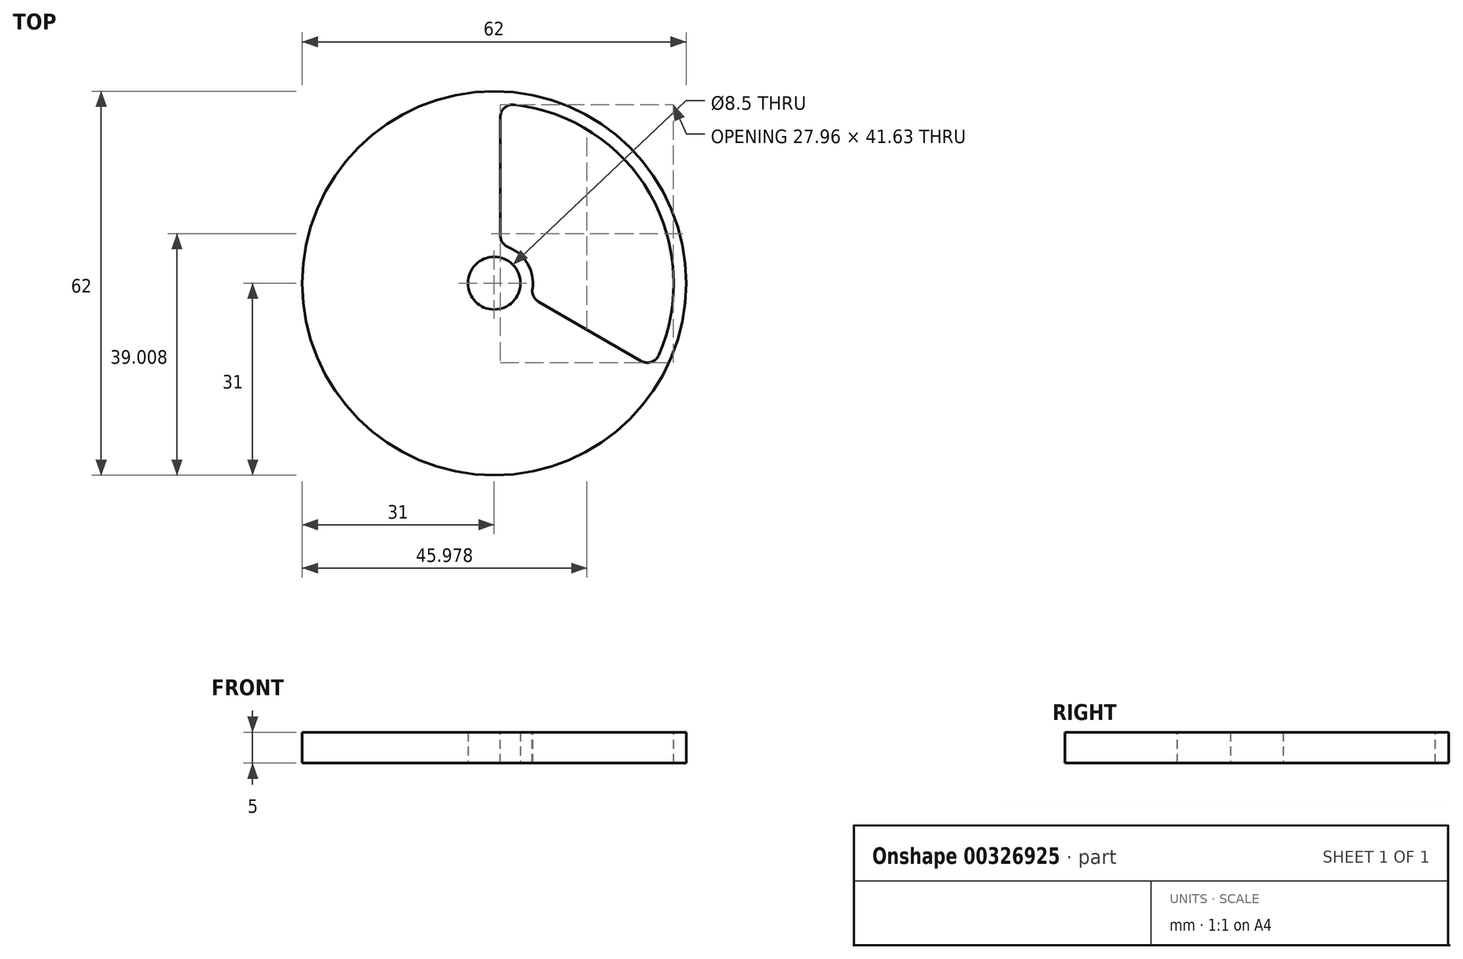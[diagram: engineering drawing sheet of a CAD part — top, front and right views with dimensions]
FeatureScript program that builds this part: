
annotation { "Feature Type Name" : "Feature", "Feature Type Description" : "" }
export const myFeature = defineFeature(function(context is Context, id is Id, definition is map)
    precondition{}
    {
        {
            var Q0;
            Q0=qCreatedBy(makeId("Top.planeOp"),FACE);
            var sketch = newSketch(context, id + "F0", { "sketchPlane" : qUnion([Q0])});
            skCircle(sketch, "E0", {"center": v(0, 0) * mm, "radius": 4.25 * mm});
            skCircle(sketch, "E1", {"center": v(0, 0) * mm, "radius": 31 * mm});
            skSolve(sketch);
        }
        {
            var Q0;
            Q0 = qSketchRegion(id + "F0", true);
            extrude(context, id + "F1", {"entities" : qUnion([Q0]), "depth" : 5 * mm});
        }
        {
            var Q0;
            Q0=makeQuery(id+"F1.opExtrude","CAP_FACE",FACE,{"disambiguationData":[OSD([sQuery(id+"F0.wireOp",EDGE,"E0"),sQuery(id+"F0.wireOp",EDGE,"E1")])],"isStart":false});
            var sketch = newSketch(context, id + "F2", { "sketchPlane" : qUnion([Q0])});
            skArc(sketch, "E2", {"start": v(5.84, -2.22) * mm, "mid": v(5.41, 3.13) * mm, "end": v(1, 6.17) * mm});
            skArc(sketch, "E3", {"start": v(25.6, -13.63) * mm, "mid": v(25.11, 14.5) * mm, "end": v(1, 28.98) * mm});
            skLineSegment(sketch, "E4", {"start": v(1, 6.17) * mm, "end": v(1, 28.98) * mm});
            skLineSegment(sketch, "E5", {"start": v(5.84, -2.22) * mm, "end": v(25.6, -13.63) * mm});
            skLineSegment(sketch, "E6", {"start": v(0, 0) * mm, "end": v(15.82, -9.14) * mm, "construction": true});
            skLineSegment(sketch, "E7", {"start": v(0, 0) * mm, "end": v(0, 20.22) * mm, "construction": true});
            skSolve(sketch);
        }
        {
            var Q0;
            Q0 = qSketchRegion(id + "F2", true);
            extrude(context, id + "F3", {"entities" : qUnion([Q0]), "operationType" : NewBodyOperationType.REMOVE, "oppositeDirection" : true, "depth" : 25 * mm});
        }
        {
            var Q0;
            Q0=makeQuery(id+"FdAd1jSosg7aUJC_1.2.F3.boolean.opBoolean","COPY",EDGE,{"derivedFrom":makeQuery(id+"FdAd1jSosg7aUJC_1.2.F3.opExtrude","SWEPT_EDGE",EDGE,{"disambiguationData":[OSD([sQuery(id+"F2.wireOp",EDGE,"E2"),sQuery(id+"F2.wireOp",EDGE,"E5")])]})});
            var Q1;
            Q1=makeQuery(id+"FdAd1jSosg7aUJC_1.2.F3.boolean.opBoolean","COPY",EDGE,{"derivedFrom":makeQuery(id+"FdAd1jSosg7aUJC_1.2.F3.opExtrude","SWEPT_EDGE",EDGE,{"disambiguationData":[OSD([sQuery(id+"F2.wireOp",EDGE,"E2"),sQuery(id+"F2.wireOp",EDGE,"E4")])]})});
            var Q2;
            Q2=makeQuery(id+"FdAd1jSosg7aUJC_1.1.F3.boolean.opBoolean","COPY",EDGE,{"derivedFrom":makeQuery(id+"FdAd1jSosg7aUJC_1.1.F3.opExtrude","SWEPT_EDGE",EDGE,{"disambiguationData":[OSD([sQuery(id+"F2.wireOp",EDGE,"E2"),sQuery(id+"F2.wireOp",EDGE,"E4")])]})});
            var Q3;
            Q3=makeQuery(id+"FdAd1jSosg7aUJC_1.1.F3.boolean.opBoolean","COPY",EDGE,{"derivedFrom":makeQuery(id+"FdAd1jSosg7aUJC_1.1.F3.opExtrude","SWEPT_EDGE",EDGE,{"disambiguationData":[OSD([sQuery(id+"F2.wireOp",EDGE,"E2"),sQuery(id+"F2.wireOp",EDGE,"E5")])]})});
            var Q4;
            Q4=makeQuery(id+"F3.boolean.opBoolean","COPY",EDGE,{"derivedFrom":makeQuery(id+"F3.opExtrude","SWEPT_EDGE",EDGE,{"disambiguationData":[OSD([sQuery(id+"F2.wireOp",EDGE,"E2"),sQuery(id+"F2.wireOp",EDGE,"E4")])]})});
            var Q5;
            Q5=makeQuery(id+"F3.boolean.opBoolean","COPY",EDGE,{"derivedFrom":makeQuery(id+"F3.opExtrude","SWEPT_EDGE",EDGE,{"disambiguationData":[OSD([sQuery(id+"F2.wireOp",EDGE,"E2"),sQuery(id+"F2.wireOp",EDGE,"E5")])]})});
            var Q6;
            Q6=makeQuery(id+"F3.boolean.opBoolean","COPY",EDGE,{"derivedFrom":makeQuery(id+"F3.opExtrude","SWEPT_EDGE",EDGE,{"disambiguationData":[OSD([sQuery(id+"F2.wireOp",EDGE,"E3"),sQuery(id+"F2.wireOp",EDGE,"E5")])]})});
            var Q7;
            Q7=makeQuery(id+"FdAd1jSosg7aUJC_1.2.F3.boolean.opBoolean","COPY",EDGE,{"derivedFrom":makeQuery(id+"FdAd1jSosg7aUJC_1.2.F3.opExtrude","SWEPT_EDGE",EDGE,{"disambiguationData":[OSD([sQuery(id+"F2.wireOp",EDGE,"E3"),sQuery(id+"F2.wireOp",EDGE,"E4")])]})});
            var Q8;
            Q8=makeQuery(id+"FdAd1jSosg7aUJC_1.2.F3.boolean.opBoolean","COPY",EDGE,{"derivedFrom":makeQuery(id+"FdAd1jSosg7aUJC_1.2.F3.opExtrude","SWEPT_EDGE",EDGE,{"disambiguationData":[OSD([sQuery(id+"F2.wireOp",EDGE,"E3"),sQuery(id+"F2.wireOp",EDGE,"E5")])]})});
            var Q9;
            Q9=makeQuery(id+"FdAd1jSosg7aUJC_1.1.F3.boolean.opBoolean","COPY",EDGE,{"derivedFrom":makeQuery(id+"FdAd1jSosg7aUJC_1.1.F3.opExtrude","SWEPT_EDGE",EDGE,{"disambiguationData":[OSD([sQuery(id+"F2.wireOp",EDGE,"E3"),sQuery(id+"F2.wireOp",EDGE,"E4")])]})});
            var Q10;
            Q10=makeQuery(id+"FdAd1jSosg7aUJC_1.1.F3.boolean.opBoolean","COPY",EDGE,{"derivedFrom":makeQuery(id+"FdAd1jSosg7aUJC_1.1.F3.opExtrude","SWEPT_EDGE",EDGE,{"disambiguationData":[OSD([sQuery(id+"F2.wireOp",EDGE,"E3"),sQuery(id+"F2.wireOp",EDGE,"E5")])]})});
            var Q11;
            Q11=makeQuery(id+"F3.boolean.opBoolean","COPY",EDGE,{"derivedFrom":makeQuery(id+"F3.opExtrude","SWEPT_EDGE",EDGE,{"disambiguationData":[OSD([sQuery(id+"F2.wireOp",EDGE,"E3"),sQuery(id+"F2.wireOp",EDGE,"E4")])]})});
            fillet(context, id + "F4", {"entities" : qUnion([Q0, Q1, Q2, Q3, Q4, Q5, Q6, Q7, Q8, Q9, Q10, Q11]), "radius" : 2 * mm, "tangentPropagation" : true, "allowEdgeOverflow" : false});
        }
    });
